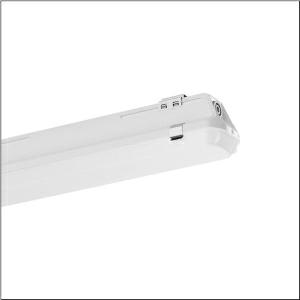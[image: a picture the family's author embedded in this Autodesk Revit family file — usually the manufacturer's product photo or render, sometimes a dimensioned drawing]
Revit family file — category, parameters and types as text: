
# Revit family: monsun_r__11_51fp109p440h_ab1f
name_source: partatom
category: Lighting Fixtures
units: mm (PartAtom-declared; Revit-internal decimal feet)

## family parameters
Cut with Voids When Loaded = No
Host = Face
Light Source = No
Part Type = Normal
Room Calculation Point = No
Round Connector Dimension = Use Diameter
Shared = No

## types (1)
- Monsun® 11 (1 x LED, 4120 lm, 22.9 W, 4000K)
    Apparent Load = 23 VA
    CIE Flux Codes = 47 77 93 94 100
    Color Rendering = 80
    Color Temperature = 4000K
    Default Elevation = 1800 mm
    Description = Monsun® 11, damp-proof luminaire, chain hanger, primary optical cover: enclosure, of PMMA, light emission: direct distribution, primary light characteristic: symmetric, installation type: suspended mounting, surface-mounted, horizontal mounting, vertical mounting, LED, rated luminous flux: 4.120lm, luminous efficacy: 180lm/W, light colour: 840, colour temperature: 4000K, control gear: ECG, with terminal, 3-pole, max. 2.5mm², mains connection: 220..240V, AC, 50/60Hz, start of lifetime: 23W, end of service life: 25W, luminaire housing, of glass-fibre reinforced polyester, uncoated, bright grey, incl. chain hanger, length: 1.590mm, width: 90mm, height: 88mm, clip for enclosure, of stainless steel (V2A), ceiling mounting element, of stainless steel (V2A), chain hanger, of stainless steel (V2A), protection rating (complete): IP66, insulation class (complete): insulation class I (protective earthing), certification: CE, ENEC, VDE, UKCA, protection symbol: D, impact resistance: IK04, permissible operating ambient temperature: -35..+40°C, standard: EN 50419, EN 60598-2-1, no direct snow, no direct sun, no direct rain, for indoor or canopied outdoor use, corresponds to IFS (International Featured Standards) requirements for safety and quality in the food industry, contact your sales advisor before using the luminaires in applications with unclear chemical exposure, large temperature fluctuations or condensation-forming humidity, LABS conformity tested according to VDMA 24364:2018-05, packaging unit: 1 piece
    Height = 89 mm
    Lamp = 1 x LED
    Lamp Light Flux = 4120 lm
    Lamp Power = 22.9 W
    Lamp count = 1
    Length = 1590 mm
    Luminous efficacy = 180 lm/W
    Manufacturer = Siteco
    ModVariant = No
    Model = 51FP109P440H
    Mounting Place = Ceiling
    Mounting Type = Surface mounted
    Number of Poles = 1
    OnlyDefault = Yes
    Power Factor = 1
    Product Name = Monsun® 11
    Product group = damp-proof luminaire
    ProductGroupID = 300
    Protection Class = Protection class I
    Protection Degree = IP 66
    RLX_Detail_Level = 1
    RLX_Emergency_Light_Flux = 0 lm
    RLX_Emergency_Type = 0
    RLX_Emergency_Type_DB = No
    RlxData = <blob elided: 88289 chars, md5=d53321f3>
    Socket = socket
    Standby Power = 0 W
    System Light Flux = 4120 lm
    System Power = 23 W
    Type Comments = Product without accessories
    Type Image = l_1004748.jpg
    URL = http://relux.com
    VarID = ---
    Voltage = 0 V
    Weight = 0.00 kg
    Width = 90 mm

## geometry (parser evidence)
native form markers: Blend x4, Sweep x12
no freeform markers — native parametric forms only
